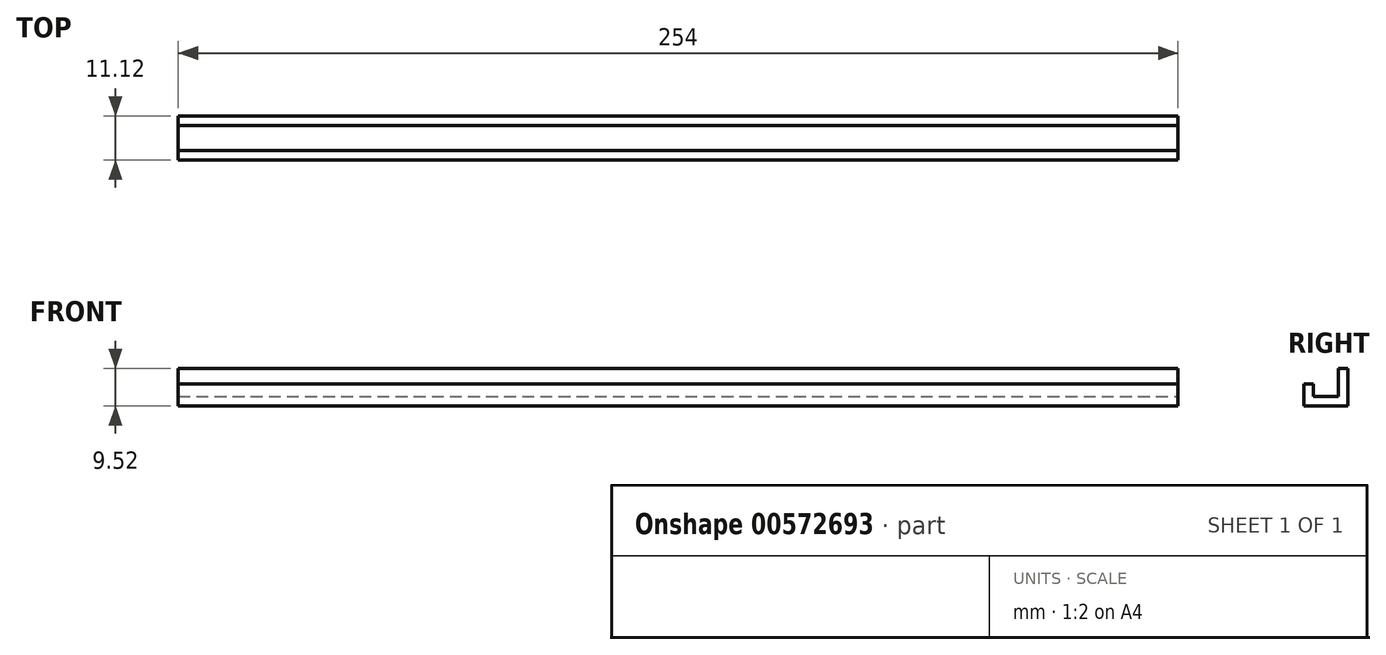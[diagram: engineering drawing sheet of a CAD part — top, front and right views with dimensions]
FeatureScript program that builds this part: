
annotation { "Feature Type Name" : "Feature", "Feature Type Description" : "" }
export const myFeature = defineFeature(function(context is Context, id is Id, definition is map)
    precondition{}
    {
        {
            var Q0;
            Q0=qCreatedBy(makeId("Right.planeOp"),FACE);
            var sketch = newSketch(context, id + "F0", { "sketchPlane" : qUnion([Q0])});
            skLineSegment(sketch, "E0.bottom", {"start": v(5.56, 4.76) * mm, "end": v(3.17, 4.76) * mm});
            skLineSegment(sketch, "E0.top", {"start": v(5.56, -4.76) * mm, "end": v(-5.56, -4.76) * mm});
            skLineSegment(sketch, "E0.left", {"start": v(5.56, 4.76) * mm, "end": v(5.56, -4.76) * mm});
            skLineSegment(sketch, "E0.right", {"start": v(-5.56, 0.8) * mm, "end": v(-5.56, -4.76) * mm});
            skPoint(sketch, "E0.middle", {"position": v(0, 0) * mm});
            skLineSegment(sketch, "E1", {"start": v(-3.17, 0.8) * mm, "end": v(-3.17, -2.38) * mm});
            skLineSegment(sketch, "E2", {"start": v(-3.17, -2.38) * mm, "end": v(3.17, -2.38) * mm});
            skLineSegment(sketch, "E3", {"start": v(3.17, -2.38) * mm, "end": v(3.17, 4.76) * mm});
            skLineSegment(sketch, "E4.trimOffspring", {"start": v(-3.17, 0.8) * mm, "end": v(-5.56, 0.8) * mm});
            skSolve(sketch);
        }
        {
            var Q0;
            Q0 = qSketchRegion(id + "F0", true);
            extrude(context, id + "F1", {"entities" : qUnion([Q0]), "oppositeDirection" : true, "depth" : 254 * mm, "offsetDistance" : 25.4 * mm});
        }
    });
